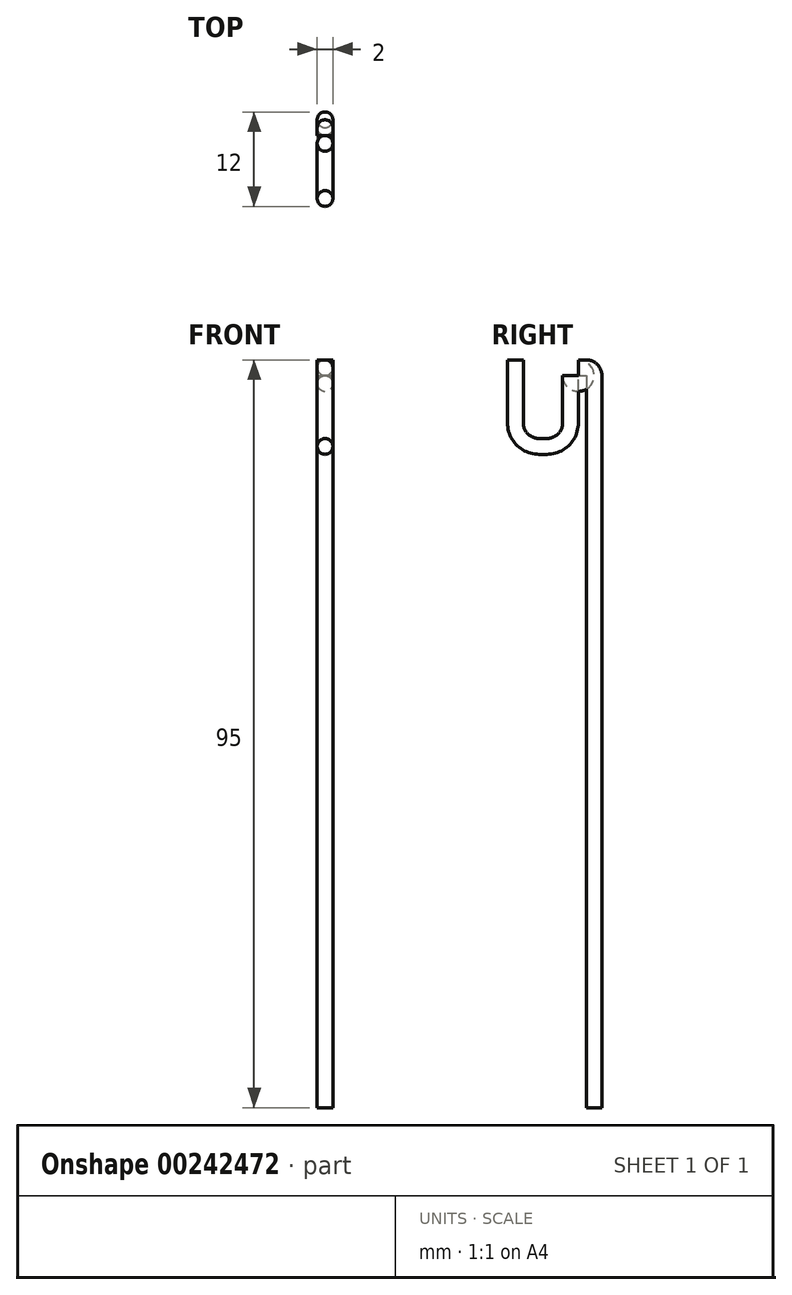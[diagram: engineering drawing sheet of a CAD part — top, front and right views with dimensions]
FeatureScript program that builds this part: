
annotation { "Feature Type Name" : "Feature", "Feature Type Description" : "" }
export const myFeature = defineFeature(function(context is Context, id is Id, definition is map)
    precondition{}
    {
        {
            var Q0;
            Q0=qCreatedBy(makeId("Right.planeOp"),FACE);
            var sketch = newSketch(context, id + "F0", { "sketchPlane" : qUnion([Q0])});
            skLineSegment(sketch, "E0", {"start": v(0, 5) * mm, "end": v(0, 98) * mm});
            skLineSegment(sketch, "E1", {"start": v(-2, 100) * mm, "end": v(-3, 100) * mm});
            skLineSegment(sketch, "E2", {"start": v(-5, 98) * mm, "end": v(-5, 92) * mm});
            skLineSegment(sketch, "E3", {"start": v(-7, 90) * mm, "end": v(-8, 90) * mm});
            skLineSegment(sketch, "E4", {"start": v(-10, 92) * mm, "end": v(-10, 100) * mm});
            skLineSegment(sketch, "E5", {"start": v(-5, 0) * mm, "end": v(-15, 0) * mm});
            skPoint(sketch, "E6.visualSharp", {"position": v(-10, 90) * mm});
            skArc(sketch, "E6.filletArc", {"start": v(-10, 92) * mm, "mid": v(-9.41, 90.59) * mm, "end": v(-8, 90) * mm});
            skPoint(sketch, "E7.visualSharp", {"position": v(-5, 90) * mm});
            skArc(sketch, "E7.filletArc", {"start": v(-7, 90) * mm, "mid": v(-5.59, 90.59) * mm, "end": v(-5, 92) * mm});
            skPoint(sketch, "E8.visualSharp", {"position": v(-5, 100) * mm});
            skArc(sketch, "E8.filletArc", {"start": v(-3, 100) * mm, "mid": v(-4.41, 99.41) * mm, "end": v(-5, 98) * mm});
            skPoint(sketch, "E9.visualSharp", {"position": v(0, 100) * mm});
            skArc(sketch, "E9.filletArc", {"start": v(0, 98) * mm, "mid": v(-0.59, 99.41) * mm, "end": v(-2, 100) * mm});
            skPoint(sketch, "E10.visualSharp", {"position": v(0, 0) * mm});
            skArc(sketch, "E10.filletArc", {"start": v(-5, 0) * mm, "mid": v(-1.46, 1.46) * mm, "end": v(0, 5) * mm});
            skPoint(sketch, "E11.end.orphan", {"position": v(-11, 100) * mm});
            skSolve(sketch);
        }
        {
            var Q0;
            Q0=qCreatedBy(makeId("Top.planeOp"),FACE);
            cPlane(context, id + "F1", {"entities" : qUnion([Q0]), "cplaneType" : CPlaneType.OFFSET, "offset" : 100 * mm, "width" : 150 * mm, "height" : 150 * mm});
        }
        {
            var Q0;
            Q0=qCreatedBy(id+"F1.planeOp",FACE);
            var sketch = newSketch(context, id + "F2", { "sketchPlane" : qUnion([Q0])});
            skPoint(sketch, "E12.start.orphan", {"position": v(0, -9.43) * mm});
            skCircle(sketch, "E13", {"center": v(0, -11) * mm, "radius": 1 * mm});
            skSolve(sketch);
        }
        {
            var Q0;
            Q0=makeQuery(id+"F2.imprint","IMPRINT",FACE,{"disambiguationData":[TD([[makeQuery(id+"F2.imprint","IMPRINT",EDGE,{"derivedFrom":sQuery(id+"F2.wireOp",EDGE,"E13")}),1.0]])]});
            var Q1;
            Q1=sQuery(id+"F0.wireOp",EDGE,"E4");
            var Q2;
            Q2=sQuery(id+"F0.wireOp",EDGE,"E6.filletArc");
            var Q3;
            Q3=sQuery(id+"F0.wireOp",EDGE,"E3");
            var Q4;
            Q4=sQuery(id+"F0.wireOp",EDGE,"E7.filletArc");
            var Q5;
            Q5=sQuery(id+"F0.wireOp",EDGE,"E2");
            var Q6;
            Q6=sQuery(id+"F0.wireOp",EDGE,"E8.filletArc");
            var Q7;
            Q7=sQuery(id+"F0.wireOp",EDGE,"E1");
            var Q8;
            Q8=sQuery(id+"F0.wireOp",EDGE,"E9.filletArc");
            var Q9;
            Q9=sQuery(id+"F0.wireOp",EDGE,"E0");
            sweep(context, id + "F3", {"profiles" : qUnion([Q0]), "path" : qUnion([Q1, Q2, Q3, Q4, Q5, Q6, Q7, Q8, Q9])});
        }
    });
